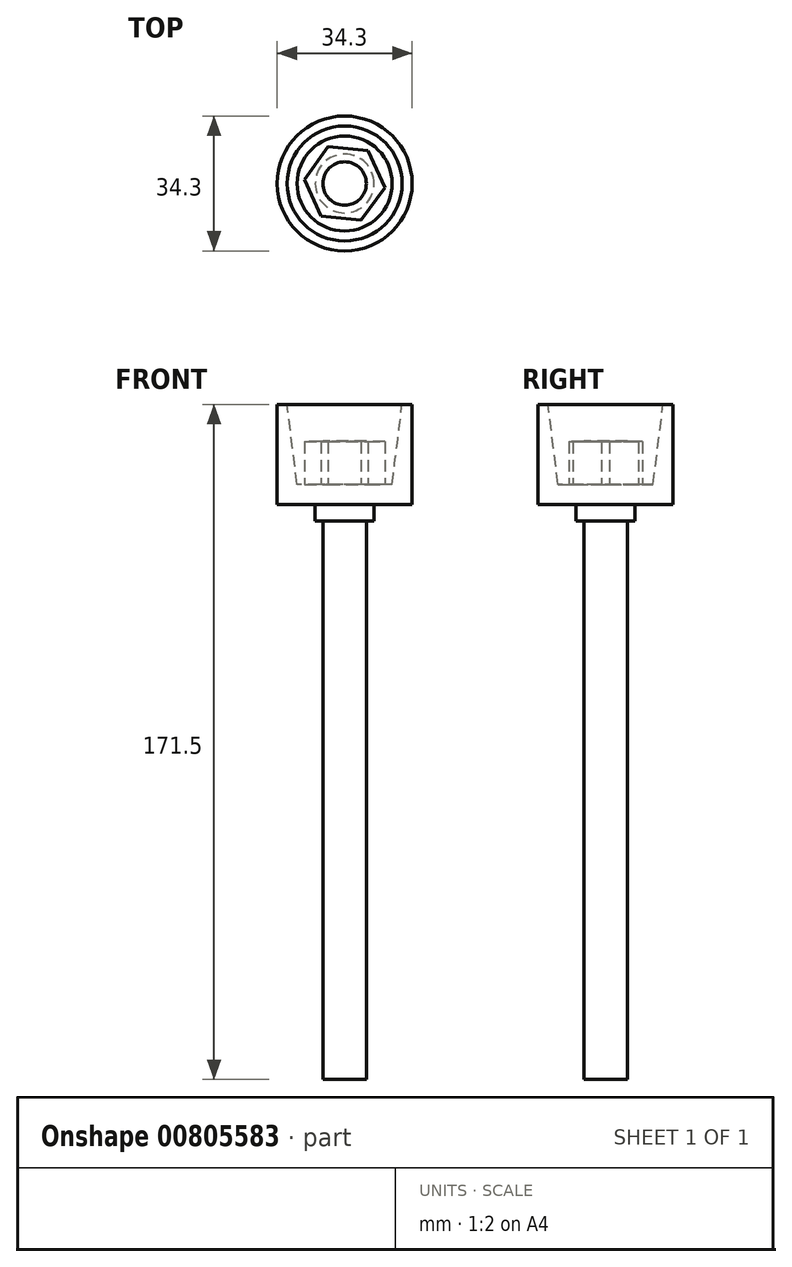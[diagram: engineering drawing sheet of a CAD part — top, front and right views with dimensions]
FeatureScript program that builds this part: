
annotation { "Feature Type Name" : "Feature", "Feature Type Description" : "" }
export const myFeature = defineFeature(function(context is Context, id is Id, definition is map)
    precondition{}
    {
        {
            var Q0;
            Q0=qCreatedBy(makeId("Top.planeOp"),FACE);
            var sketch = newSketch(context, id + "F0", { "sketchPlane" : qUnion([Q0])});
            skCircle(sketch, "E0", {"center": v(0, 0) * mm, "radius": 5.52 * mm});
            skSolve(sketch);
        }
        {
            var Q0;
            Q0 = qSketchRegion(id + "F0", true);
            extrude(context, id + "F1", {"entities" : qUnion([Q0]), "depth" : 20.32 * mm, "offsetDistance" : 25.4 * mm, "hasSecondDirection" : true, "secondDirectionOppositeDirection" : true, "secondDirectionDepth" : 141.86 * mm});
        }
        {
            var Q0;
            Q0=qCreatedBy(makeId("Top.planeOp"),FACE);
            var sketch = newSketch(context, id + "F2", { "sketchPlane" : qUnion([Q0])});
            skCircle(sketch, "E1", {"center": v(0, 0) * mm, "radius": 7.47 * mm});
            skCircle(sketch, "E2.0", {"center": v(0, 0) * mm, "radius": 5.52 * mm});
            skSolve(sketch);
        }
        {
            var Q0;
            Q0 = qSketchRegion(id + "F2", true);
            extrude(context, id + "F3", {"entities" : qUnion([Q0]), "operationType" : NewBodyOperationType.ADD, "depth" : 4.24 * mm, "offsetDistance" : 25.4 * mm});
        }
        {
            var Q0;
            Q0=makeQuery(id+"F3.opExtrude","CAP_FACE",FACE,{"disambiguationData":[OSD([sQuery(id+"F2.wireOp",EDGE,"E1"),sQuery(id+"F2.wireOp",EDGE,"E2.0")])],"isStart":false});
            var sketch = newSketch(context, id + "F4", { "sketchPlane" : qUnion([Q0])});
            skCircle(sketch, "E3", {"center": v(0, 0) * mm, "radius": 17.15 * mm});
            skSolve(sketch);
        }
        {
            var Q0;
            Q0 = qSketchRegion(id + "F4", true);
            extrude(context, id + "F5", {"entities" : qUnion([Q0]), "operationType" : NewBodyOperationType.ADD, "depth" : 5.08 * mm, "offsetDistance" : 25.4 * mm});
        }
        {
            var Q0;
            Q0=makeQuery(id+"F5.opExtrude","CAP_FACE",FACE,{"disambiguationData":[OSD([sQuery(id+"F4.wireOp",EDGE,"E3")])],"isStart":false});
            var sketch = newSketch(context, id + "F6", { "sketchPlane" : qUnion([Q0])});
            skCircle(sketch, "E4.cCircle", {"center": v(0, 0) * mm, "radius": 8.88 * mm, "construction": true});
            skLineSegment(sketch, "E4.0", {"start": v(10.2, -1.03) * mm, "end": v(4.2, -9.35) * mm});
            skLineSegment(sketch, "E4.1", {"start": v(4.2, -9.35) * mm, "end": v(-6, -8.32) * mm});
            skLineSegment(sketch, "E4.2", {"start": v(-6, -8.32) * mm, "end": v(-10.2, 1.03) * mm});
            skLineSegment(sketch, "E4.3", {"start": v(-10.2, 1.03) * mm, "end": v(-4.2, 9.35) * mm});
            skLineSegment(sketch, "E4.4", {"start": v(-4.2, 9.35) * mm, "end": v(6, 8.32) * mm});
            skLineSegment(sketch, "E4.5", {"start": v(6, 8.32) * mm, "end": v(10.2, -1.03) * mm});
            skPoint(sketch, "E4.0.midPoint", {"position": v(7.2, -5.19) * mm});
            skSolve(sketch);
        }
        {
            var Q0;
            Q0 = qSketchRegion(id + "F6", true);
            extrude(context, id + "F7", {"entities" : qUnion([Q0]), "operationType" : NewBodyOperationType.ADD, "depth" : 10.87 * mm, "offsetDistance" : 25.4 * mm});
        }
        {
            var Q0;
            Q0=makeQuery(id+"F5.opExtrude","CAP_FACE",FACE,{"disambiguationData":[OSD([sQuery(id+"F4.wireOp",EDGE,"E3")])],"isStart":false});
            var sketch = newSketch(context, id + "F8", { "sketchPlane" : qUnion([Q0])});
            skCircle(sketch, "E5.0", {"center": v(0, 0) * mm, "radius": 17.15 * mm});
            skCircle(sketch, "E6.0", {"center": v(0, 0) * mm, "radius": 14.6 * mm});
            skSolve(sketch);
        }
        {
            var Q0;
            Q0 = qSketchRegion(id + "F8", true);
            extrude(context, id + "F9", {"entities" : qUnion([Q0]), "operationType" : NewBodyOperationType.ADD, "depth" : 20.32 * mm, "offsetDistance" : 25.4 * mm});
        }
        {
            var Q0;
            Q0=qCreatedBy(makeId("Right.planeOp"),FACE);
            var sketch = newSketch(context, id + "F10", { "sketchPlane" : qUnion([Q0])});
            skLineSegment(sketch, "E7", {"start": v(-17.15, 4.24) * mm, "end": v(-17.15, 29.64) * mm});
            skLineSegment(sketch, "E8", {"start": v(17.15, 29.64) * mm, "end": v(17.15, 4.24) * mm});
            skLineSegment(sketch, "E9.0", {"start": v(-14.6, 9.32) * mm, "end": v(-12.07, 9.32) * mm});
            skLineSegment(sketch, "E10", {"start": v(-14.6, 9.32) * mm, "end": v(-14.6, 29.64) * mm});
            skLineSegment(sketch, "E11", {"start": v(-14.6, 29.64) * mm, "end": v(-12.07, 9.32) * mm});
            skPoint(sketch, "E12.orphan", {"position": v(14.6, 9.32) * mm});
            skLineSegment(sketch, "E13", {"start": v(0, 9.19) * mm, "end": v(0, 21.25) * mm, "construction": true});
            skSolve(sketch);
        }
        {
            var Q0;
            Q0 = qSketchRegion(id + "F10", true);
            var Q1;
            Q1=sQuery(id+"F10.wireOp",EDGE,"E13");
            revolve(context, id + "F11", {"operationType" : NewBodyOperationType.ADD, "surfaceOperationType" : NewSurfaceOperationType.NEW, "entities" : qUnion([Q0]), "axis" : qUnion([Q1]), "revolveType" : RevolveType.FULL});
        }
    });
